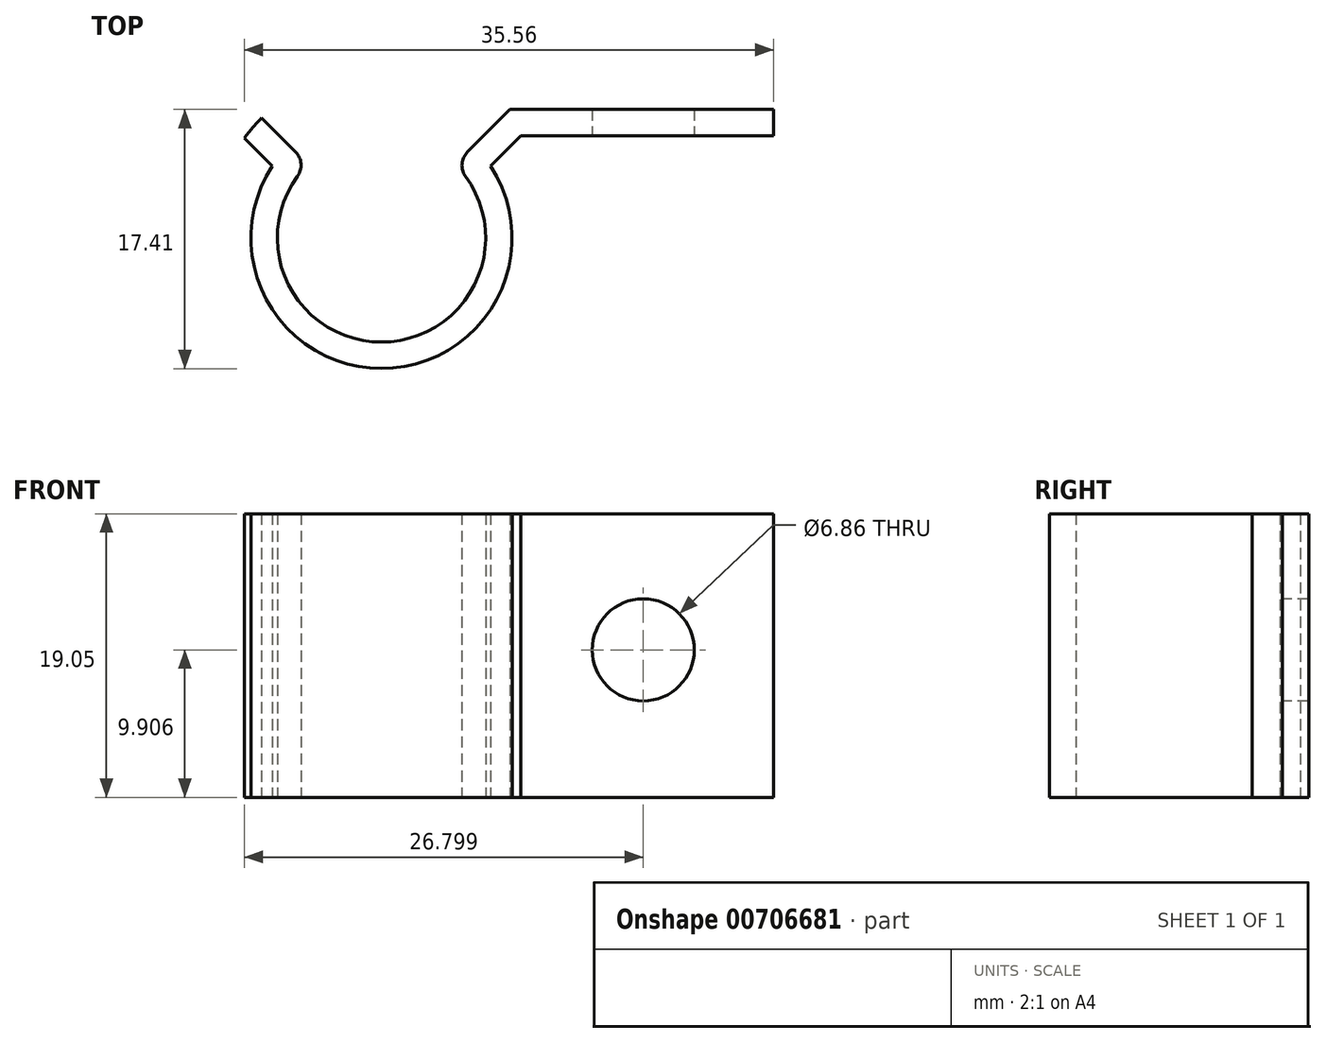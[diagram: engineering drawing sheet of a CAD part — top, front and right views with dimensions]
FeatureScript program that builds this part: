
annotation { "Feature Type Name" : "Feature", "Feature Type Description" : "" }
export const myFeature = defineFeature(function(context is Context, id is Id, definition is map)
    precondition{}
    {
        {
            var Q0;
            Q0=qCreatedBy(makeId("Top.planeOp"),FACE);
            var sketch = newSketch(context, id + "F0", { "sketchPlane" : qUnion([Q0])});
            skArc(sketch, "E0", {"start": v(-5.65, 4.13) * mm, "mid": v(0, -7) * mm, "end": v(5.65, 4.13) * mm});
            skArc(sketch, "E1.0", {"start": v(-7.34, 4.82) * mm, "mid": v(0, -8.78) * mm, "end": v(7.34, 4.82) * mm});
            skLineSegment(sketch, "E2", {"start": v(-5.78, 5.78) * mm, "end": v(-8.06, 8.06) * mm});
            skLineSegment(sketch, "E3", {"start": v(8.63, 8.63) * mm, "end": v(5.78, 5.78) * mm});
            skLineSegment(sketch, "E4.0", {"start": v(-7.34, 4.82) * mm, "end": v(-9.21, 6.7) * mm});
            skLineSegment(sketch, "E4.1", {"start": v(9.37, 6.86) * mm, "end": v(7.34, 4.82) * mm});
            skArc(sketch, "E5", {"start": v(-8.06, 8.06) * mm, "mid": v(-8.66, 7.4) * mm, "end": v(-9.21, 6.7) * mm});
            skLineSegment(sketch, "E6", {"start": v(8.63, 8.63) * mm, "end": v(26.35, 8.63) * mm});
            skLineSegment(sketch, "E7", {"start": v(26.35, 8.63) * mm, "end": v(26.35, 6.86) * mm});
            skLineSegment(sketch, "E8", {"start": v(26.35, 6.86) * mm, "end": v(9.37, 6.86) * mm});
            skPoint(sketch, "E9.visualSharp", {"position": v(-4.95, 4.95) * mm});
            skArc(sketch, "E9.filletArc", {"start": v(-5.65, 4.13) * mm, "mid": v(-5.41, 4.98) * mm, "end": v(-5.78, 5.78) * mm});
            skPoint(sketch, "E10.visualSharp", {"position": v(4.95, 4.95) * mm});
            skArc(sketch, "E10.filletArc", {"start": v(5.78, 5.78) * mm, "mid": v(5.41, 4.98) * mm, "end": v(5.65, 4.13) * mm});
            skSolve(sketch);
        }
        {
            var Q0;
            Q0 = qSketchRegion(id + "F0", true);
            extrude(context, id + "F1", {"entities" : qUnion([Q0]), "depth" : 19.05 * mm, "offsetDistance" : 25.4 * mm});
        }
        {
            var Q0;
            Q0=makeQuery(id+"F1.opExtrude","SWEPT_FACE",FACE,{"disambiguationData":[OSD([sQuery(id+"F0.wireOp",EDGE,"E8")])]});
            var sketch = newSketch(context, id + "F2", { "sketchPlane" : qUnion([Q0])});
            skCircle(sketch, "E11", {"center": v(17.59, 9.9) * mm, "radius": 3.43 * mm});
            skSolve(sketch);
        }
        {
            var Q0;
            Q0 = qSketchRegion(id + "F2", true);
            extrude(context, id + "F3", {"entities" : qUnion([Q0]), "operationType" : NewBodyOperationType.REMOVE, "oppositeDirection" : true, "depth" : 25.4 * mm, "offsetDistance" : 25.4 * mm});
        }
    });
